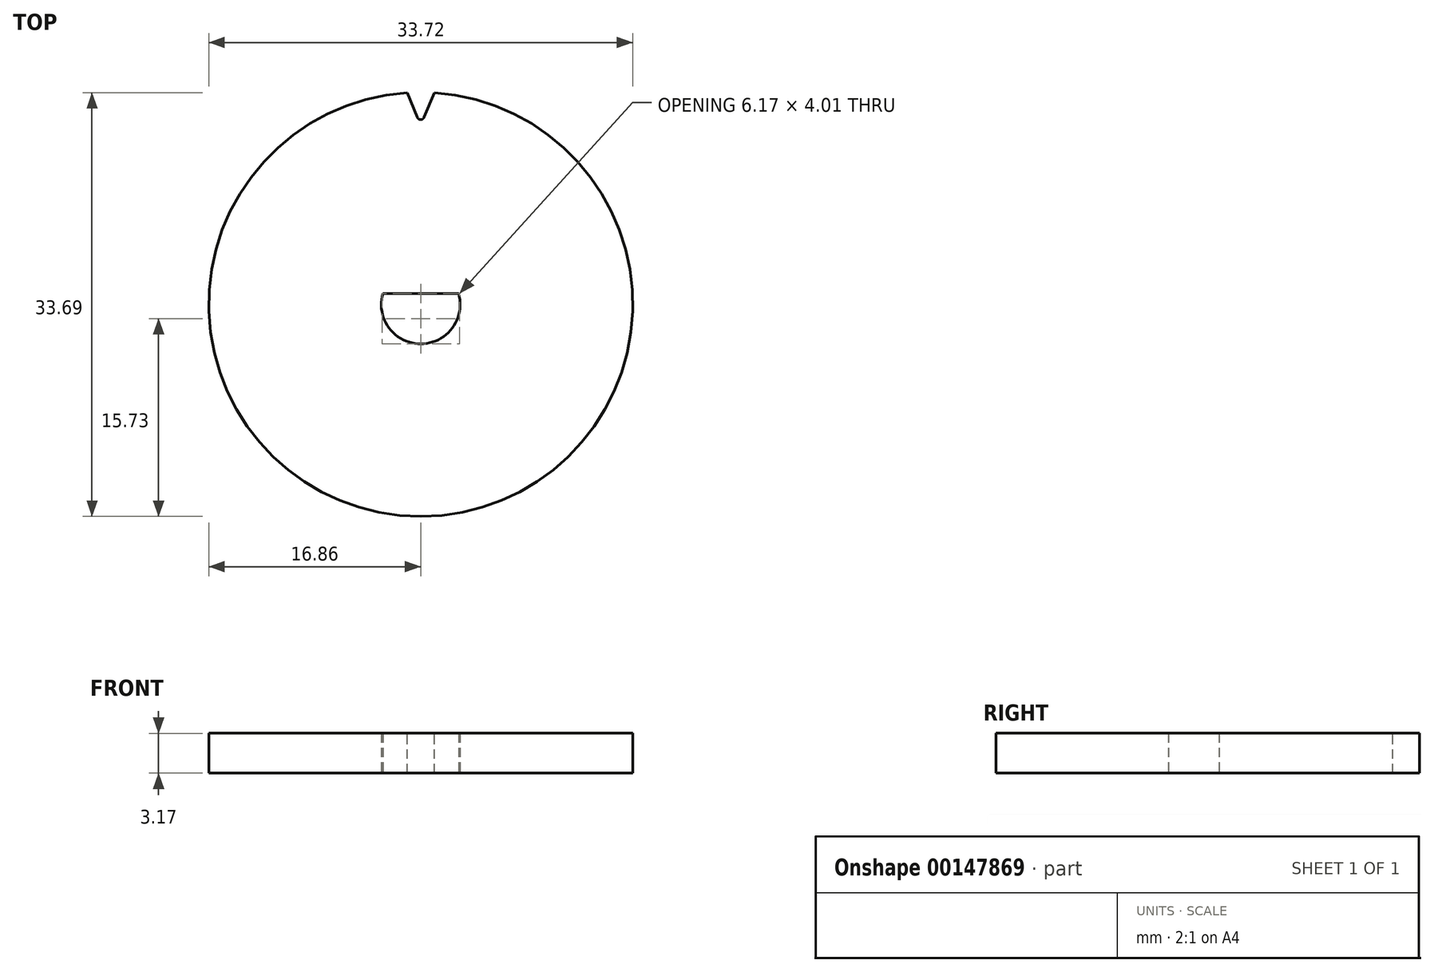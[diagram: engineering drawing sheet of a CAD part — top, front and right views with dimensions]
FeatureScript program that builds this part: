
annotation { "Feature Type Name" : "Feature", "Feature Type Description" : "" }
export const myFeature = defineFeature(function(context is Context, id is Id, definition is map)
    precondition{}
    {
        {
            var Q0;
            Q0=qCreatedBy(makeId("Top.planeOp"),FACE);
            var sketch = newSketch(context, id + "F0", { "sketchPlane" : qUnion([Q0])});
            skCircle(sketch, "E0", {"center": v(0, 0) * mm, "radius": 16.86 * mm});
            skLineSegment(sketch, "E1", {"start": v(0, 0) * mm, "end": v(0, 0.88) * mm, "construction": true});
            skLineSegment(sketch, "E2", {"start": v(-3.01, 0.88) * mm, "end": v(3.01, 0.88) * mm});
            skArc(sketch, "E3", {"start": v(-3.01, 0.88) * mm, "mid": v(0, -3.14) * mm, "end": v(3.01, 0.88) * mm});
            skSolve(sketch);
        }
        {
            var Q0;
            Q0=makeQuery(id+"F0.imprint","IMPRINT",FACE,{"disambiguationData":[TD([[makeQuery(id+"F0.imprint","IMPRINT",EDGE,{"derivedFrom":sQuery(id+"F0.wireOp",EDGE,"d7zeTPih-CRss-xDOh-gPdP-rmPCdwzH7cdN.left")}),1.0]])]});
            var Q1;
            Q1=makeQuery(id+"F0.imprint","IMPRINT",FACE,{"disambiguationData":[TD([[makeQuery(id+"F0.imprint","IMPRINT",EDGE,{"derivedFrom":sQuery(id+"F0.wireOp",EDGE,"E0")}),1.0]])]});
            extrude(context, id + "F1", {"entities" : qUnion([Q0, Q1]), "depth" : 3.17 * mm});
        }
        {
            var Q0;
            Q0=makeQuery(id+"F1.opExtrude","CAP_FACE",FACE,{"disambiguationData":[OSD([sQuery(id+"F0.wireOp",EDGE,"d7zeTPih-CRss-xDOh-gPdP-rmPCdwzH7cdN.left"),sQuery(id+"F0.wireOp",EDGE,"d7zeTPih-CRss-xDOh-gPdP-rmPCdwzH7cdN.right"),sQuery(id+"F0.wireOp",EDGE,"ScfBMfkV-s1yN-Ls9R-SGr5-fEyGpD6zak8e"),sQuery(id+"F0.wireOp",EDGE,"xnxmVwjl-FvSF-m7sj-be2U-u85gZZGoORGZ"),sQuery(id+"F0.wireOp",EDGE,"E0")])],"isStart":false});
            var sketch = newSketch(context, id + "F2", { "sketchPlane" : qUnion([Q0])});
            skLineSegment(sketch, "E4", {"start": v(0, 0) * mm, "end": v(0, 16.86) * mm, "construction": true});
            skLineSegment(sketch, "E5", {"start": v(0, 0) * mm, "end": v(0.72, 16.85) * mm, "construction": true});
            skArc(sketch, "E6", {"start": v(1.08, 16.83) * mm, "mid": v(0, 16.86) * mm, "end": v(-1.08, 16.83) * mm});
            skLineSegment(sketch, "E7", {"start": v(-1.08, 16.83) * mm, "end": v(-0.28, 14.88) * mm});
            skLineSegment(sketch, "E8", {"start": v(1.08, 16.83) * mm, "end": v(0.28, 14.88) * mm});
            skPoint(sketch, "E9", {"position": v(0.68, 15.85) * mm});
            skArc(sketch, "E10", {"start": v(-0.28, 14.88) * mm, "mid": v(0, 14.7) * mm, "end": v(0.28, 14.88) * mm});
            skSolve(sketch);
        }
        {
            var Q0;
            Q0=qSketchRegion(id+"F2",true);
            var Q1;
            Q1=makeQuery(id+"F1.opExtrude","CAP_FACE",FACE,{"disambiguationData":[OSD([sQuery(id+"F0.wireOp",EDGE,"d7zeTPih-CRss-xDOh-gPdP-rmPCdwzH7cdN.left"),sQuery(id+"F0.wireOp",EDGE,"d7zeTPih-CRss-xDOh-gPdP-rmPCdwzH7cdN.right"),sQuery(id+"F0.wireOp",EDGE,"ScfBMfkV-s1yN-Ls9R-SGr5-fEyGpD6zak8e"),sQuery(id+"F0.wireOp",EDGE,"xnxmVwjl-FvSF-m7sj-be2U-u85gZZGoORGZ"),sQuery(id+"F0.wireOp",EDGE,"E0")])],"isStart":true});
            extrude(context, id + "F3", {"entities" : qUnion([Q0]), "operationType" : NewBodyOperationType.REMOVE, "endBound" : BoundingType.UP_TO_SURFACE, "oppositeDirection" : true, "endBoundEntityFace" : qUnion([Q1]), "depth" : 25.4 * mm});
        }
    });
